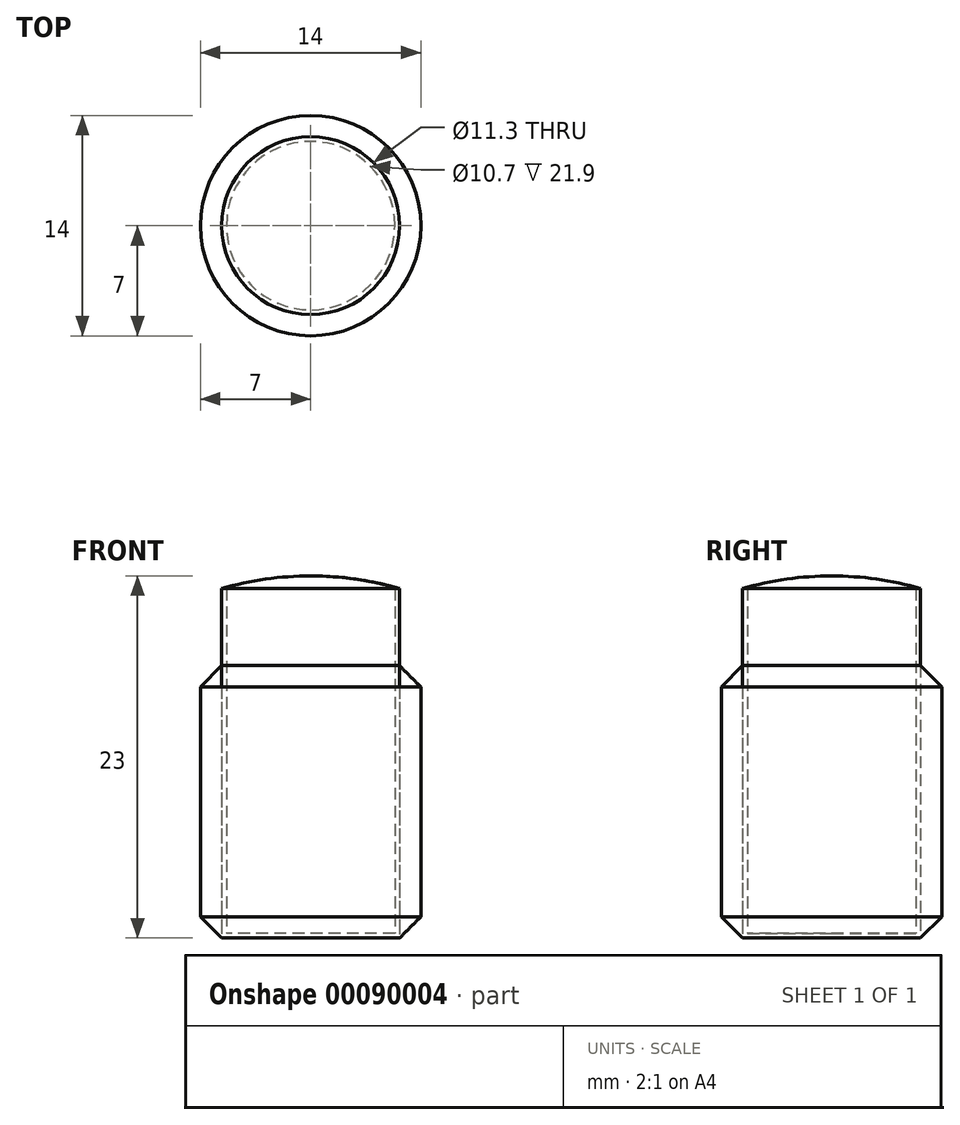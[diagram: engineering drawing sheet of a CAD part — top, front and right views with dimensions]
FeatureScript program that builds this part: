
annotation { "Feature Type Name" : "Feature", "Feature Type Description" : "" }
export const myFeature = defineFeature(function(context is Context, id is Id, definition is map)
    precondition{}
    {
        {
            var Q0;
            Q0=qCreatedBy(makeId("Top.planeOp"),FACE);
            var sketch = newSketch(context, id + "F0", { "sketchPlane" : qUnion([Q0])});
            skCircle(sketch, "E0", {"center": v(0, 0) * mm, "radius": 5.65 * mm});
            skSolve(sketch);
        }
        {
            var Q0;
            Q0 = qSketchRegion(id + "F0", true);
            extrude(context, id + "F1", {"entities" : qUnion([Q0]), "depth" : 22.2 * mm});
        }
        {
            var Q0;
            Q0=makeQuery(id+"F1.opExtrude","CAP_FACE",FACE,{"disambiguationData":[OSD([sQuery(id+"F0.wireOp",EDGE,"E0")])],"isStart":false});
            shell(context, id + "F2", {"entities" : qUnion([Q0]), "thickness" : 0.3 * mm});
        }
        {
            var Q0;
            Q0=qCreatedBy(makeId("Front.planeOp"),FACE);
            var sketch = newSketch(context, id + "F3", { "sketchPlane" : qUnion([Q0])});
            skLineSegment(sketch, "E1", {"start": v(0, 22.2) * mm, "end": v(0, 23) * mm});
            skLineSegment(sketch, "E2.0", {"start": v(0, 22.2) * mm, "end": v(5.65, 22.2) * mm});
            skPoint(sketch, "E3.orphan", {"position": v(-5.65, 22.2) * mm});
            skArc(sketch, "E4", {"start": v(5.65, 22.2) * mm, "mid": v(2.85, 22.8) * mm, "end": v(0, 23) * mm});
            skLineSegment(sketch, "E5", {"start": v(0, 23) * mm, "end": v(-5.65, 23) * mm, "construction": true});
            skSolve(sketch);
        }
        {
            var Q0;
            Q0 = qSketchRegion(id + "F3", true);
            var Q1;
            Q1=sQuery(id+"F3.wireOp",EDGE,"E1");
            revolve(context, id + "F4", {"entities" : qUnion([Q0]), "axis" : qUnion([Q1]), "revolveType" : RevolveType.FULL});
        }
        {
            var Q0;
            Q0=qCreatedBy(makeId("Top.planeOp"),FACE);
            var sketch = newSketch(context, id + "F5", { "sketchPlane" : qUnion([Q0])});
            skCircle(sketch, "E6", {"center": v(0, 0) * mm, "radius": 7 * mm});
            skCircle(sketch, "E7.0", {"center": v(0, 0) * mm, "radius": 5.65 * mm});
            skSolve(sketch);
        }
        {
            var Q0;
            Q0 = qSketchRegion(id + "F5", true);
            extrude(context, id + "F6", {"entities" : qUnion([Q0]), "depth" : 17.3 * mm});
        }
        {
            var Q0;
            Q0=qCreatedBy(makeId("Front.planeOp"),FACE);
            var sketch = newSketch(context, id + "F7", { "sketchPlane" : qUnion([Q0])});
            skLineSegment(sketch, "E8.0", {"start": v(-7, 17.3) * mm, "end": v(-5.65, 17.3) * mm});
            skLineSegment(sketch, "E9.0", {"start": v(-7, 0) * mm, "end": v(-5.65, 0) * mm});
            skLineSegment(sketch, "E10", {"start": v(-7, 0) * mm, "end": v(-7, 1.35) * mm});
            skLineSegment(sketch, "E11", {"start": v(-7, 1.35) * mm, "end": v(-5.65, 0) * mm});
            skLineSegment(sketch, "E12", {"start": v(-7, 17.3) * mm, "end": v(-7, 15.95) * mm});
            skLineSegment(sketch, "E13", {"start": v(-7, 15.95) * mm, "end": v(-5.65, 17.3) * mm});
            skLineSegment(sketch, "E14", {"start": v(-5.65, 0) * mm, "end": v(-5.65, 22.2) * mm, "construction": true});
            skLineSegment(sketch, "E15", {"start": v(0, 0) * mm, "end": v(0, 22.2) * mm, "construction": true});
            skSolve(sketch);
        }
        {
            var Q0;
            Q0 = qSketchRegion(id + "F7", true);
            var Q1;
            Q1=sQuery(id+"F7.wireOp",EDGE,"E15");
            revolve(context, id + "F8", {"operationType" : NewBodyOperationType.REMOVE, "entities" : qUnion([Q0]), "axis" : qUnion([Q1]), "revolveType" : RevolveType.FULL, "oppositeDirection" : true});
        }
    });
